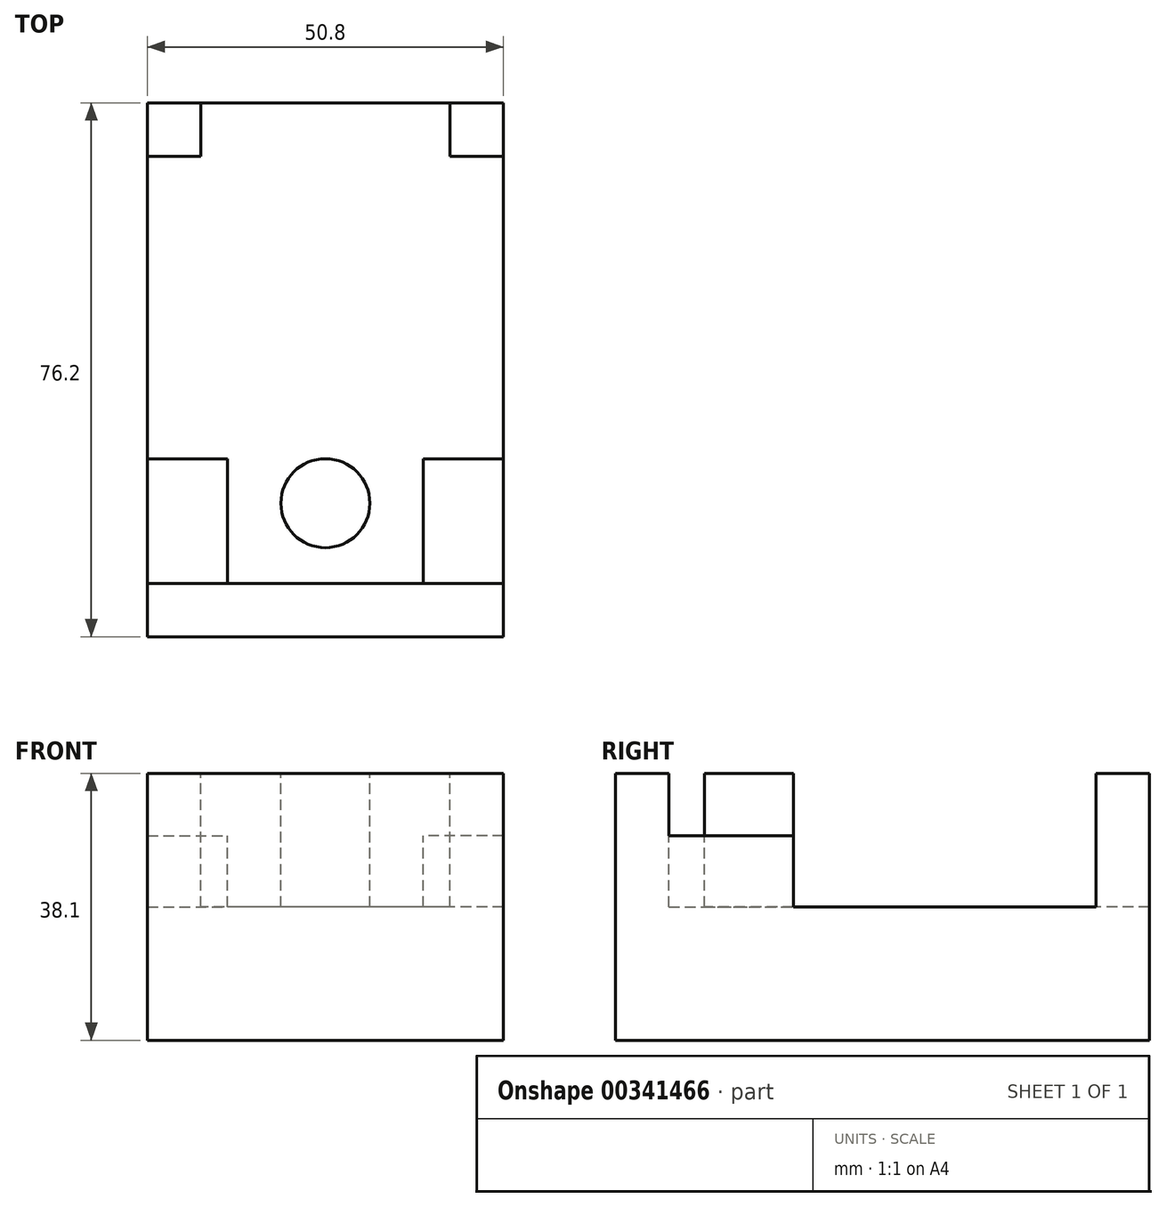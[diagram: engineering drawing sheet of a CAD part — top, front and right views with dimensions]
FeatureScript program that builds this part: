
annotation { "Feature Type Name" : "Feature", "Feature Type Description" : "" }
export const myFeature = defineFeature(function(context is Context, id is Id, definition is map)
    precondition{}
    {
        {
            var Q0;
            Q0=qCreatedBy(makeId("Top.planeOp"),FACE);
            var sketch = newSketch(context, id + "F0", { "sketchPlane" : qUnion([Q0])});
            skLineSegment(sketch, "E0.bottom", {"start": v(25.4, -38.1) * mm, "end": v(-25.4, -38.1) * mm});
            skLineSegment(sketch, "E0.top", {"start": v(25.4, 38.1) * mm, "end": v(-25.4, 38.1) * mm});
            skLineSegment(sketch, "E0.left", {"start": v(25.4, -38.1) * mm, "end": v(25.4, 38.1) * mm});
            skLineSegment(sketch, "E0.right", {"start": v(-25.4, -38.1) * mm, "end": v(-25.4, 38.1) * mm});
            skPoint(sketch, "E0.middle", {"position": v(0, 0) * mm});
            skSolve(sketch);
        }
        {
            var Q0;
            Q0=makeQuery(id+"F0.imprint","IMPRINT",FACE,{"disambiguationData":[TD([[makeQuery(id+"F0.imprint","IMPRINT",EDGE,{"derivedFrom":sQuery(id+"F0.wireOp",EDGE,"E0.bottom")}),-1.0]])]});
            extrude(context, id + "F1", {"entities" : qUnion([Q0]), "endBound" : BoundingType.SYMMETRIC, "depth" : 38.1 * mm});
        }
        {
            var Q0;
            Q0=makeQuery(id+"F1.opExtrude","CAP_FACE",FACE,{"disambiguationData":[OSD([sQuery(id+"F0.wireOp",EDGE,"E0.bottom"),sQuery(id+"F0.wireOp",EDGE,"E0.top"),sQuery(id+"F0.wireOp",EDGE,"E0.left"),sQuery(id+"F0.wireOp",EDGE,"E0.right")])],"isStart":false});
            var sketch = newSketch(context, id + "F2", { "sketchPlane" : qUnion([Q0])});
            skLineSegment(sketch, "E1", {"start": v(-25.4, 38.1) * mm, "end": v(-25.4, 30.48) * mm});
            skLineSegment(sketch, "E2", {"start": v(-25.4, 30.48) * mm, "end": v(-17.78, 30.48) * mm});
            skLineSegment(sketch, "E3", {"start": v(-17.78, 30.48) * mm, "end": v(-17.78, 38.1) * mm});
            skLineSegment(sketch, "E4", {"start": v(-17.78, 38.1) * mm, "end": v(-25.4, 38.1) * mm});
            skLineSegment(sketch, "E5.bottom", {"start": v(25.4, 38.1) * mm, "end": v(17.78, 38.1) * mm});
            skLineSegment(sketch, "E5.top", {"start": v(25.4, 30.48) * mm, "end": v(17.78, 30.48) * mm});
            skLineSegment(sketch, "E5.left", {"start": v(25.4, 38.1) * mm, "end": v(25.4, 30.48) * mm});
            skLineSegment(sketch, "E5.right", {"start": v(17.78, 38.1) * mm, "end": v(17.78, 30.48) * mm});
            skLineSegment(sketch, "E6.bottom", {"start": v(25.4, -38.1) * mm, "end": v(13.97, -38.1) * mm});
            skLineSegment(sketch, "E6.top", {"start": v(25.4, -12.7) * mm, "end": v(13.97, -12.7) * mm});
            skLineSegment(sketch, "E6.left", {"start": v(25.4, -38.1) * mm, "end": v(25.4, -12.7) * mm});
            skLineSegment(sketch, "E6.right", {"start": v(13.97, -38.1) * mm, "end": v(13.97, -12.7) * mm});
            skLineSegment(sketch, "E7.bottom", {"start": v(-25.4, -38.1) * mm, "end": v(-13.97, -38.1) * mm});
            skLineSegment(sketch, "E7.top", {"start": v(-25.4, -12.7) * mm, "end": v(-13.97, -12.7) * mm});
            skLineSegment(sketch, "E7.left", {"start": v(-25.4, -38.1) * mm, "end": v(-25.4, -12.7) * mm});
            skLineSegment(sketch, "E7.right", {"start": v(-13.97, -38.1) * mm, "end": v(-13.97, -12.7) * mm});
            skLineSegment(sketch, "E8.bottom", {"start": v(25.4, -38.1) * mm, "end": v(-25.4, -38.1) * mm});
            skLineSegment(sketch, "E8.top", {"start": v(25.4, -30.48) * mm, "end": v(-25.4, -30.48) * mm});
            skLineSegment(sketch, "E8.left", {"start": v(25.4, -38.1) * mm, "end": v(25.4, -30.48) * mm});
            skLineSegment(sketch, "E8.right", {"start": v(-25.4, -38.1) * mm, "end": v(-25.4, -30.48) * mm});
            skSolve(sketch);
        }
        {
            var Q0;
            {var subQ3=sQuery(id+"F2.wireOp",EDGE,"E2");Q0=makeQuery(id+"F2.imprint","IMPRINT",FACE,{"disambiguationData":[TD([[makeQuery(id+"F2.imprint","IMPRINT",EDGE,{"derivedFrom":subQ3}),-1.0]])]});}
            var sketch = newSketch(context, id + "F3", { "sketchPlane" : qUnion([Q0])});
            skCircle(sketch, "E9", {"center": v(0, -19.05) * mm, "radius": 6.35 * mm});
            skSolve(sketch);
        }
        {
            var Q0;
            Q0=makeQuery(id+"F3.imprint","IMPRINT",FACE,{"disambiguationData":[TD([[makeQuery(id+"F3.imprint","IMPRINT",EDGE,{"derivedFrom":sQuery(id+"F3.wireOp",EDGE,"E9")}),-1.0]])]});
            extrude(context, id + "F4", {"entities" : qUnion([Q0]), "operationType" : NewBodyOperationType.REMOVE, "oppositeDirection" : true, "depth" : 19.05 * mm});
        }
        {
            var Q0;
            {var subQ0=sQuery(id+"F2.wireOp",EDGE,"E6.top");Q0=makeQuery(id+"F2.imprint","IMPRINT",FACE,{"disambiguationData":[TD([[makeQuery(id+"F2.imprint","IMPRINT",EDGE,{"derivedFrom":subQ0}),1.0]])]});}
            var Q1;
            {var subQ0=sQuery(id+"F2.wireOp",EDGE,"E7.top");Q1=makeQuery(id+"F2.imprint","IMPRINT",FACE,{"disambiguationData":[TD([[makeQuery(id+"F2.imprint","IMPRINT",EDGE,{"derivedFrom":subQ0}),-1.0]])]});}
            extrude(context, id + "F5", {"entities" : qUnion([Q0, Q1]), "operationType" : NewBodyOperationType.REMOVE, "oppositeDirection" : true, "depth" : 8.9 * mm});
        }
    });
